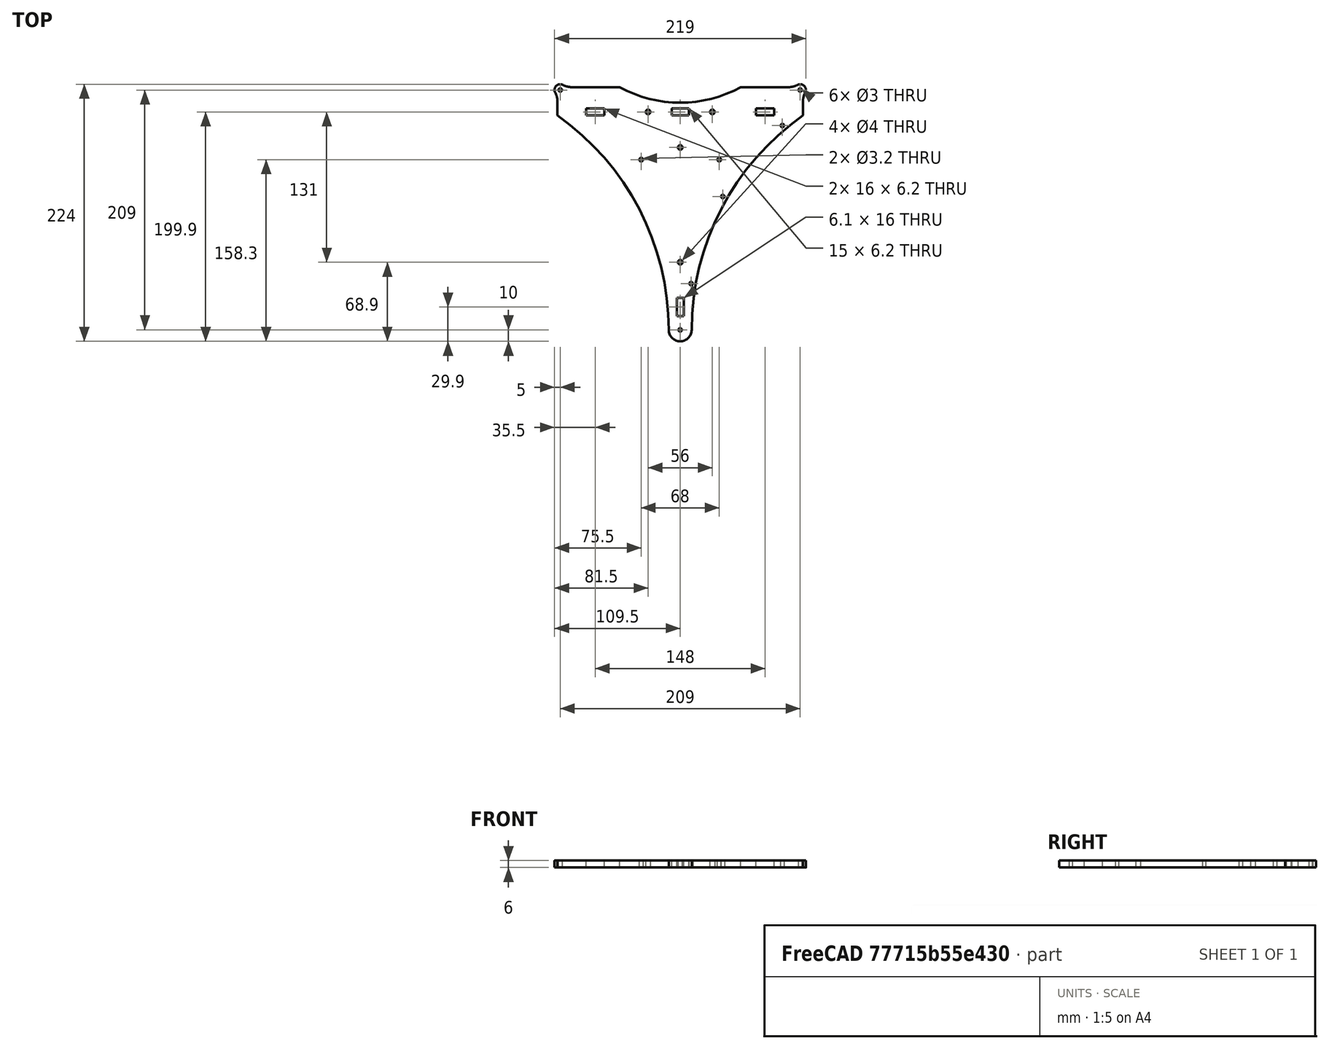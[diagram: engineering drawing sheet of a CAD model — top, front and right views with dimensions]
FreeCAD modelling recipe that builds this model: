
FCSTD DOCUMENT  (FreeCAD 0.17R13541 (Git))
Label: xx_xxx_bed
License: All rights reserved
LicenseURL: http://en.wikipedia.org/wiki/All_rights_reserved
objects: Sketcher::SketchObject×1, PartDesign::Pad×1, PartDesign::Body×1
note: 4 computed .brp shape members not serialized (recipe doc carries the construction recipe); baked Part::Feature solids carry a one-line shape summary decoded from their .brp

FEATURE [Sketcher::SketchObject] Sketch042
  MapMode = 5
  Support = -> [XY_Plane]
  sketch-geometry (42):
    g0: Circle CenterX=34 CenterY=43.8 CenterZ=0 NormalX=0 NormalY=0 NormalZ=-1 AngleXU=0 Radius=1.6
    g1: ArcOfCircle CenterX=0 CenterY=-104.5 CenterZ=0 NormalX=0 NormalY=0 NormalZ=1 AngleXU=0 Radius=10 StartAngle=3.14159 EndAngle=6.28319
    g2: Circle CenterX=9.53018 CenterY=-64.1499 CenterZ=0 NormalX=0 NormalY=0 NormalZ=-1 AngleXU=0 Radius=1.5
    g3: ArcOfCircle CenterX=-104.5 CenterY=104.5 CenterZ=0 NormalX=0 NormalY=0 NormalZ=1 AngleXU=0 Radius=5 StartAngle=1.06544 EndAngle=3.64695
    g4: Circle CenterX=-104.5 CenterY=104.5 CenterZ=0 NormalX=0 NormalY=0 NormalZ=-1 AngleXU=0 Radius=1.5
    g5: ArcOfCircle CenterX=238.367 CenterY=-104.5 CenterZ=0 NormalX=0 NormalY=0 NormalZ=1 AngleXU=0 Radius=228.367 StartAngle=2.1837 EndAngle=3.14159
    g6: LineSegment StartX=-52.7171 StartY=107 StartZ=0 EndX=-94.8175 EndY=107 EndZ=0
    g7: Circle CenterX=28 CenterY=85.4 CenterZ=0 NormalX=0 NormalY=0 NormalZ=-1 AngleXU=0 Radius=2
    g8: LineSegment StartX=-7.5 StartY=82.3 StartZ=0 EndX=7.5 EndY=82.3 EndZ=0
    g9: ArcOfCircle CenterX=-122 CenterY=94.8175 CenterZ=0 NormalX=0 NormalY=0 NormalZ=1 AngleXU=0 Radius=15 StartAngle=0 EndAngle=0.505361
    g10: LineSegment StartX=82 StartY=88.5 StartZ=0 EndX=66 EndY=88.5 EndZ=0
    g11: Circle CenterX=0 CenterY=-104.5 CenterZ=0 NormalX=0 NormalY=0 NormalZ=-1 AngleXU=0 Radius=1.5
    g12: LineSegment StartX=-3.05 StartY=-76.6 StartZ=0 EndX=-3.05 EndY=-92.6 EndZ=0
    g13: LineSegment StartX=3.05 StartY=-92.6 StartZ=0 EndX=3.05 EndY=-76.6 EndZ=0
    g14: ArcOfCircle CenterX=-238.367 CenterY=-104.5 CenterZ=0 NormalX=0 NormalY=0 NormalZ=1 AngleXU=0 Radius=228.367 StartAngle=0 EndAngle=0.957892
    g15: LineSegment StartX=-66 StartY=88.5 StartZ=0 EndX=-82 EndY=88.5 EndZ=0
    g16: LineSegment StartX=66 StartY=88.5 StartZ=0 EndX=66 EndY=82.3 EndZ=0
    g17: LineSegment StartX=-66 StartY=82.3 StartZ=0 EndX=-66 EndY=88.5 EndZ=0
    g18: ArcOfCircle CenterX=104.5 CenterY=104.5 CenterZ=0 NormalX=0 NormalY=0 NormalZ=1 AngleXU=0 Radius=5 StartAngle=5.77782 EndAngle=8.35934
    g19: LineSegment StartX=7.5 StartY=82.3 StartZ=0 EndX=7.5 EndY=88.5 EndZ=0
    g20: LineSegment StartX=-7.5 StartY=88.5 StartZ=0 EndX=-7.5 EndY=82.3 EndZ=0
    g21: Circle CenterX=-28 CenterY=85.4 CenterZ=0 NormalX=0 NormalY=0 NormalZ=-1 AngleXU=0 Radius=2
    g22: Circle CenterX=-34 CenterY=43.8 CenterZ=0 NormalX=0 NormalY=0 NormalZ=-1 AngleXU=0 Radius=1.6
    g23: LineSegment StartX=107 StartY=82.3 StartZ=0 EndX=107 EndY=94.8175 EndZ=0
    g24: LineSegment StartX=-107 StartY=94.8175 StartZ=0 EndX=-107 EndY=82.3 EndZ=0
    g25: LineSegment StartX=-82 StartY=82.3 StartZ=0 EndX=-66 EndY=82.3 EndZ=0
    g26: ArcOfCircle CenterX=0 CenterY=202.372 CenterZ=0 NormalX=0 NormalY=0 NormalZ=1 AngleXU=0 Radius=108.972 StartAngle=4.20744 EndAngle=5.21734
    g27: Circle CenterX=0 CenterY=54.4 CenterZ=0 NormalX=0 NormalY=0 NormalZ=-1 AngleXU=0 Radius=2
    g28: LineSegment StartX=-82 StartY=88.5 StartZ=0 EndX=-82 EndY=82.3 EndZ=0
    g29: LineSegment StartX=-3.05 StartY=-92.6 StartZ=0 EndX=3.05 EndY=-92.6 EndZ=0
    g30: LineSegment StartX=82 StartY=82.3 StartZ=0 EndX=82 EndY=88.5 EndZ=0
    g31: ArcOfCircle CenterX=-94.8175 CenterY=122 CenterZ=0 NormalX=0 NormalY=0 NormalZ=1 AngleXU=0 Radius=15 StartAngle=4.20703 EndAngle=4.71239
    g32: LineSegment StartX=7.5 StartY=88.5 StartZ=0 EndX=-7.5 EndY=88.5 EndZ=0
    g33: Circle CenterX=0 CenterY=-45.6 CenterZ=0 NormalX=0 NormalY=0 NormalZ=-1 AngleXU=0 Radius=2
    g34: ArcOfCircle CenterX=94.8175 CenterY=122 CenterZ=0 NormalX=0 NormalY=0 NormalZ=1 AngleXU=0 Radius=15 StartAngle=4.71239 EndAngle=5.21775
    g35: LineSegment StartX=94.8175 StartY=107 StartZ=0 EndX=52.7171 EndY=107 EndZ=0
    g36: LineSegment StartX=66 StartY=82.3 StartZ=0 EndX=82 EndY=82.3 EndZ=0
    g37: LineSegment StartX=3.05 StartY=-76.6 StartZ=0 EndX=-3.05 EndY=-76.6 EndZ=0
    g38: Circle CenterX=104.5 CenterY=104.5 CenterZ=0 NormalX=0 NormalY=0 NormalZ=-1 AngleXU=0 Radius=1.5
    g39: Circle CenterX=37.1313 CenterY=11.6836 CenterZ=0 NormalX=0 NormalY=0 NormalZ=-1 AngleXU=0 Radius=1.5
    g40: Circle CenterX=89.0044 CenterY=73.5036 CenterZ=0 NormalX=0 NormalY=0 NormalZ=-1 AngleXU=0 Radius=1.5
    g41: ArcOfCircle CenterX=122 CenterY=94.8175 CenterZ=0 NormalX=0 NormalY=0 NormalZ=1 AngleXU=0 Radius=15 StartAngle=2.63623 EndAngle=3.14159
  constraints (30):
    c: Coincident(g3,g9)
    c: Coincident(g14,g24)
    c: Coincident(g24,g9)
    c: Coincident(g3,g31)
    c: Coincident(g31,g6)
    c: Coincident(g28,g25)
    c: Coincident(g28,g15)
    c: Coincident(g17,g25)
    c: Coincident(g17,g15)
    c: Coincident(g26,g6)
    c: Coincident(g1,g14)
    c: Coincident(g20,g8)
    c: Coincident(g32,g20)
    c: Coincident(g12,g29)
    c: Coincident(g37,g12)
    c: Coincident(g13,g29)
    c: Coincident(g13,g37)
    c: Coincident(g8,g19)
    c: Coincident(g19,g32)
    c: Coincident(g1,g5)
    c: Coincident(g26,g35)
    c: Coincident(g16,g36)
    c: Coincident(g16,g10)
    c: Coincident(g30,g36)
    c: Coincident(g30,g10)
    c: Coincident(g34,g35)
    c: Coincident(g18,g34)
    c: Coincident(g5,g23)
    c: Coincident(g41,g23)
    c: Coincident(g18,g41)
FEATURE [PartDesign::Pad] Pad
  Length = 6
  Length2 = 100
  Profile = -> Sketch042
  Type = 0
FEATURE [PartDesign::Body] Body
  Group = -> [Sketch042,Pad]
  Origin = -> Origin
  Tip = -> Pad
